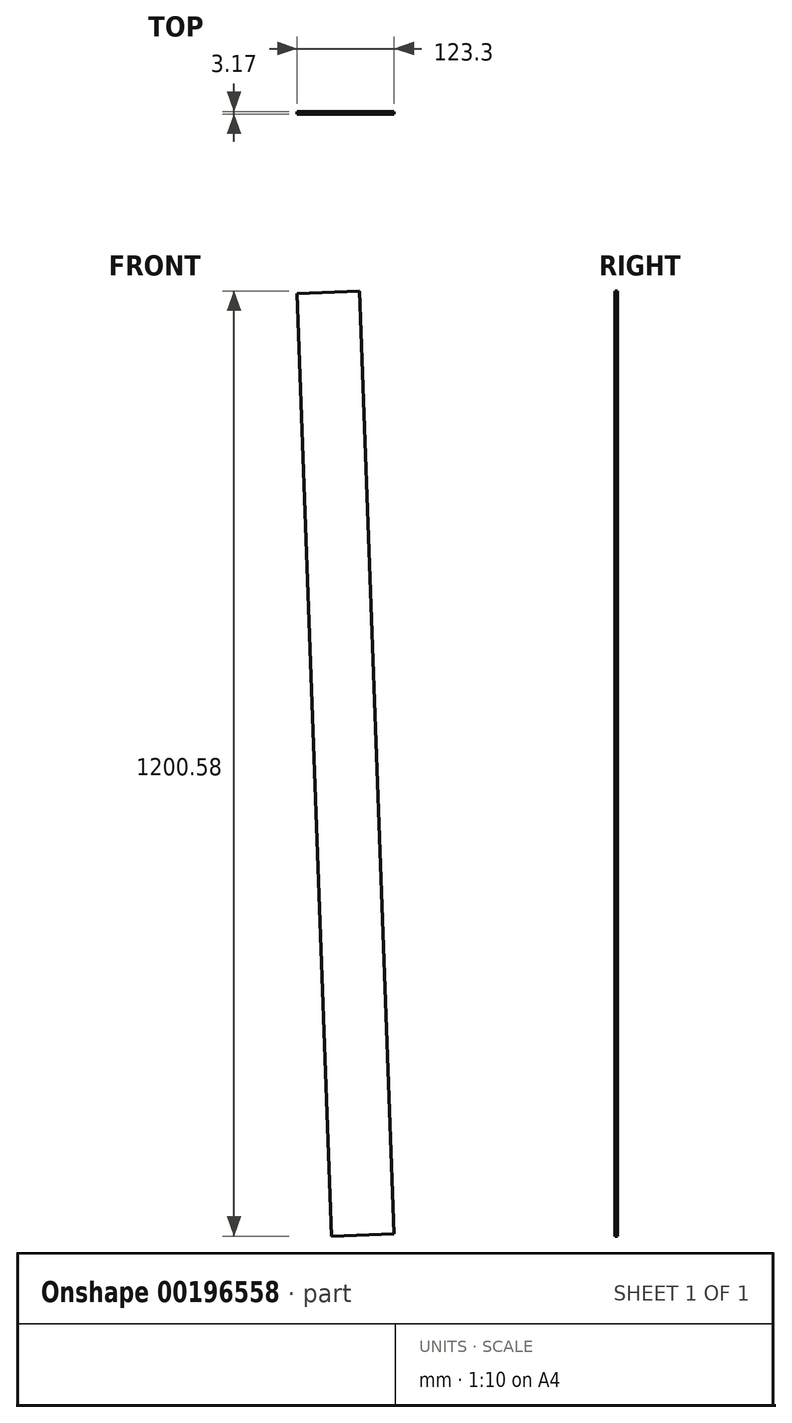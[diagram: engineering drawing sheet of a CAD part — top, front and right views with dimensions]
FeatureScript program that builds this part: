
annotation { "Feature Type Name" : "Feature", "Feature Type Description" : "" }
export const myFeature = defineFeature(function(context is Context, id is Id, definition is map)
    precondition{}
    {
        {
            var Q0;
            Q0=qCreatedBy(makeId("Front.planeOp"),FACE);
            var sketch = newSketch(context, id + "F0", { "sketchPlane" : qUnion([Q0])});
            skLineSegment(sketch, "E0", {"start": v(61.65, -597.37) * mm, "end": v(-17.67, -600.29) * mm});
            skLineSegment(sketch, "E1", {"start": v(-17.67, -600.29) * mm, "end": v(-61.65, 597.37) * mm});
            skLineSegment(sketch, "E2", {"start": v(-61.65, 597.37) * mm, "end": v(17.67, 600.29) * mm});
            skLineSegment(sketch, "E3", {"start": v(17.67, 600.29) * mm, "end": v(61.65, -597.37) * mm});
            skSolve(sketch);
        }
        {
            var Q0;
            Q0=makeQuery(id+"F0.imprint","IMPRINT",FACE,{"disambiguationData":[TD([[makeQuery(id+"F0.imprint","IMPRINT",EDGE,{"derivedFrom":sQuery(id+"F0.wireOp",EDGE,"E0")}),-1.0]])]});
            var Q1;
            Q1=sQuery(id+"F0.wireOp",EDGE,"E0");
            var Q2;
            Q2=sQuery(id+"F0.wireOp",EDGE,"E1");
            var Q3;
            Q3=sQuery(id+"F0.wireOp",EDGE,"E2");
            var Q4;
            Q4=sQuery(id+"F0.wireOp",EDGE,"E3");
            extrude(context, id + "F1", {"entities" : qUnion([Q0]), "surfaceEntities" : qUnion([Q1, Q2, Q3, Q4]), "depth" : 3.17 * mm});
        }
    });
